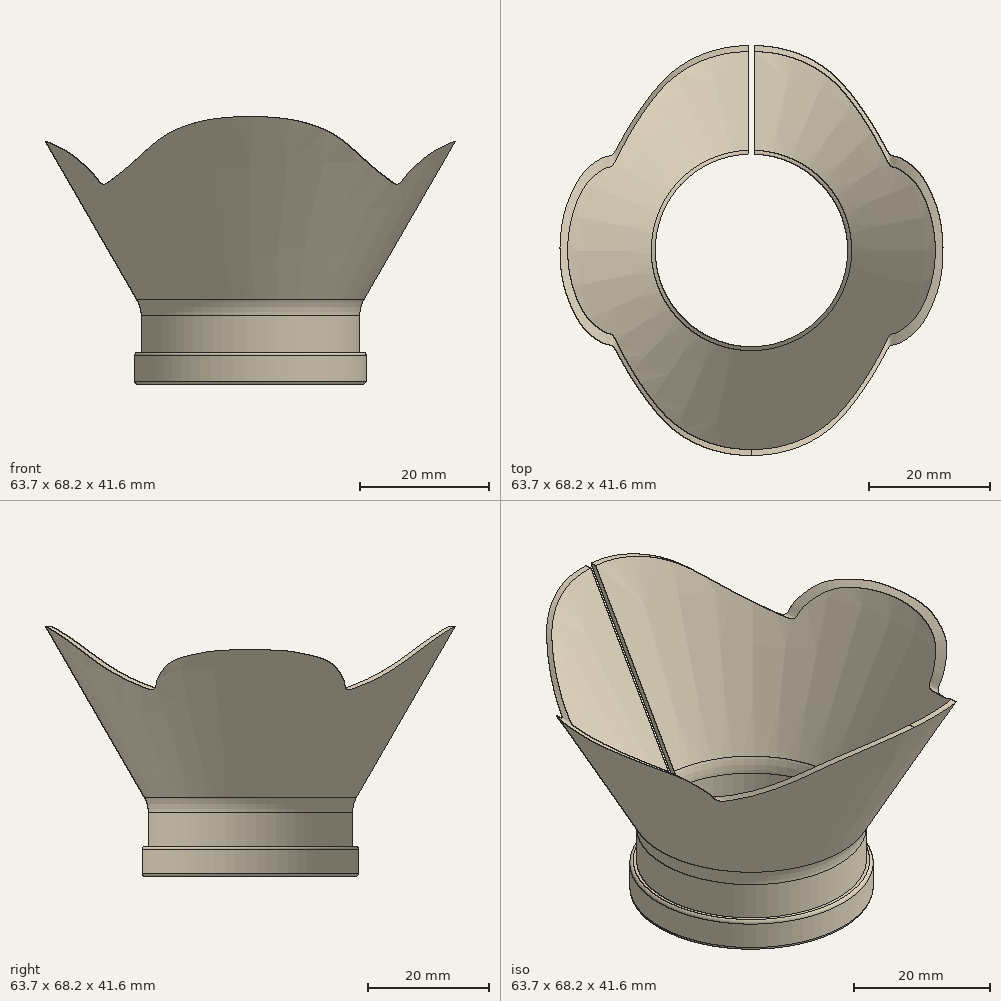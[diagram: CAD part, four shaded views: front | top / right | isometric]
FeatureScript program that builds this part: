
annotation { "Feature Type Name" : "Feature", "Feature Type Description" : "" }
export const myFeature = defineFeature(function(context is Context, id is Id, definition is map)
    precondition{}
    {
        {
            var Q0;
            Q0=qCreatedBy(makeId("Top.planeOp"),FACE);
            var sketch = newSketch(context, id + "F0", { "sketchPlane" : qUnion([Q0])});
            skCircle(sketch, "E0", {"center": v(0, 0) * mm, "radius": 16 * mm});
            skCircle(sketch, "E1.0", {"center": v(0, 0) * mm, "radius": 17 * mm});
            skSolve(sketch);
        }
        {
            var Q0;
            Q0 = qSketchRegion(id + "F0", true);
            extrude(context, id + "F1", {"entities" : qUnion([Q0]), "depth" : 12 * mm});
        }
        {
            var Q0;
            Q0=qCreatedBy(makeId("Front.planeOp"),FACE);
            var sketch = newSketch(context, id + "F2", { "sketchPlane" : qUnion([Q0])});
            skLineSegment(sketch, "E2", {"start": v(0, 0) * mm, "end": v(0, 61.93) * mm, "construction": true});
            skLineSegment(sketch, "E3.0", {"start": v(-17, 12) * mm, "end": v(17, 12) * mm, "construction": true});
            skLineSegment(sketch, "E4", {"start": v(17, 12) * mm, "end": v(34.32, 42) * mm});
            skLineSegment(sketch, "E5", {"start": v(34.32, 42) * mm, "end": v(33.57, 42.43) * mm});
            skLineSegment(sketch, "E6", {"start": v(33.57, 42.43) * mm, "end": v(16, 12) * mm});
            skLineSegment(sketch, "E7", {"start": v(16, 12) * mm, "end": v(17, 12) * mm});
            skLineSegment(sketch, "E8", {"start": v(17, 12) * mm, "end": v(17, 0) * mm, "construction": true});
            skLineSegment(sketch, "E9.bottom", {"start": v(17, 5) * mm, "end": v(18, 5) * mm});
            skLineSegment(sketch, "E9.top", {"start": v(17, 0) * mm, "end": v(18, 0) * mm});
            skLineSegment(sketch, "E9.left", {"start": v(17, 5) * mm, "end": v(17, 0) * mm});
            skLineSegment(sketch, "E9.right", {"start": v(18, 5) * mm, "end": v(18, 0) * mm});
            skSolve(sketch);
        }
        {
            var Q0;
            Q0 = qSketchRegion(id + "F2", true);
            var Q1;
            Q1=sQuery(id+"F2.wireOp",EDGE,"E2");
            revolve(context, id + "F3", {"operationType" : NewBodyOperationType.ADD, "entities" : qUnion([Q0]), "axis" : qUnion([Q1]), "revolveType" : RevolveType.FULL});
        }
        {
            var Q0;
            Q0=qCreatedBy(makeId("Front.planeOp"),FACE);
            var sketch = newSketch(context, id + "F4", { "sketchPlane" : qUnion([Q0])});
            skLineSegment(sketch, "E10.bottom", {"start": v(-60, 60.13) * mm, "end": v(60, 60.13) * mm});
            skLineSegment(sketch, "E10.top", {"start": v(-60, 27) * mm, "end": v(-45.7, 27) * mm});
            skLineSegment(sketch, "E10.left", {"start": v(-60, 60.13) * mm, "end": v(-60, 27) * mm});
            skLineSegment(sketch, "E10.right", {"start": v(60, 60.13) * mm, "end": v(60, 27) * mm});
            skPoint(sketch, "E11.0.internal.snap0", {"position": v(0, 60.13) * mm});
            skFitSpline(sketch, "E11", {"points": [v(0, 41.6) * mm, v(7.62, 40.86) * mm, v(12.88, 38.86) * mm, v(16.15, 36.34) * mm, v(19.48, 33.36) * mm, v(21.5, 31.79) * mm, v(22.87, 31.07) * mm, v(23.9, 32.05) * mm, v(25.66, 33.9) * mm, v(28.18, 35.99) * mm, v(30.49, 37.2) * mm, v(32.97, 37.6) * mm, v(45.7, 27) * mm], "startDerivative": vector(73.9, 0.28) * mm, "endDerivative": vector(56.85, -72.76) * mm});
            skFitSpline(sketch, "E12.MirrorCS", {"points": [v(0, 41.6) * mm, v(-7.62, 40.86) * mm, v(-12.88, 38.86) * mm, v(-16.15, 36.34) * mm, v(-19.48, 33.36) * mm, v(-21.5, 31.79) * mm, v(-22.87, 31.07) * mm, v(-23.9, 32.05) * mm, v(-25.66, 33.9) * mm, v(-28.18, 35.99) * mm, v(-30.49, 37.2) * mm, v(-32.97, 37.6) * mm, v(-45.7, 27) * mm], "startDerivative": vector(-73.9, 0.28) * mm, "endDerivative": vector(-56.85, -72.76) * mm});
            skLineSegment(sketch, "E13.trimOffspring", {"start": v(45.7, 27) * mm, "end": v(60, 27) * mm});
            skSolve(sketch);
        }
        {
            var Q0;
            Q0 = qSketchRegion(id + "F4", true);
            extrude(context, id + "F5", {"entities" : qUnion([Q0]), "operationType" : NewBodyOperationType.REMOVE, "endBound" : BoundingType.THROUGH_ALL, "oppositeDirection" : true, "depth" : 25 * mm, "hasSecondDirection" : true, "secondDirectionBound" : SecondDirectionBoundingType.THROUGH_ALL, "secondDirectionOppositeDirection" : false, "secondDirectionDepth" : 25 * mm});
        }
        {
            var Q0;
            Q0=qCreatedBy(makeId("Top.planeOp"),FACE);
            var sketch = newSketch(context, id + "F6", { "sketchPlane" : qUnion([Q0])});
            skLineSegment(sketch, "E14.bottom", {"start": v(0.5, 0) * mm, "end": v(-0.5, 0) * mm});
            skLineSegment(sketch, "E14.top", {"start": v(0.5, 50) * mm, "end": v(-0.5, 50) * mm});
            skLineSegment(sketch, "E14.left", {"start": v(0.5, 0) * mm, "end": v(0.5, 50) * mm});
            skLineSegment(sketch, "E14.right", {"start": v(-0.5, 0) * mm, "end": v(-0.5, 50) * mm});
            skSolve(sketch);
        }
        {
            var Q0;
            Q0 = qSketchRegion(id + "F6", true);
            extrude(context, id + "F7", {"entities" : qUnion([Q0]), "operationType" : NewBodyOperationType.REMOVE, "endBound" : BoundingType.THROUGH_ALL, "depth" : 25 * mm});
        }
        {
            var Q0;
            Q0=makeQuery(id+"F3.boolean.opBoolean","MERGE",EDGE,{"derivedFrom":[makeQuery(id+"F1.opExtrude","CAP_EDGE",EDGE,{"disambiguationData":[OSD([sQuery(id+"F0.wireOp",EDGE,"E0")])],"isStart":false}),makeQuery(id+"F3.opRevolve","SWEPT_EDGE",EDGE,{"disambiguationData":[OSD([sQuery(id+"F2.wireOp",EDGE,"E6"),sQuery(id+"F2.wireOp",EDGE,"E7")])]})]});
            fillet(context, id + "F8", {"entities" : qUnion([Q0]), "radius" : 5 * mm, "tangentPropagation" : true, "allowEdgeOverflow" : false});
        }
        {
            var Q0;
            Q0=makeQuery(id+"F3.boolean.opBoolean","MERGE",EDGE,{"derivedFrom":[makeQuery(id+"F1.opExtrude","CAP_EDGE",EDGE,{"disambiguationData":[OSD([sQuery(id+"F0.wireOp",EDGE,"E1.0")])],"isStart":false}),makeQuery(id+"F3.opRevolve","SWEPT_EDGE",EDGE,{"disambiguationData":[OSD([sQuery(id+"F2.wireOp",EDGE,"E4"),sQuery(id+"F2.wireOp",EDGE,"E7")])]})]});
            fillet(context, id + "F9", {"entities" : qUnion([Q0]), "radius" : 5 * mm, "tangentPropagation" : true, "allowEdgeOverflow" : false});
        }
        {
            var Q0;
            Q0=makeQuery(id+"F3.opRevolve","SWEPT_EDGE",EDGE,{"disambiguationData":[OSD([sQuery(id+"F2.wireOp",EDGE,"E9.bottom"),sQuery(id+"F2.wireOp",EDGE,"E9.left")])]});
            var Q1;
            Q1=makeQuery(id+"F3.opRevolve","SWEPT_EDGE",EDGE,{"disambiguationData":[OSD([sQuery(id+"F2.wireOp",EDGE,"E9.bottom"),sQuery(id+"F2.wireOp",EDGE,"E9.right")])]});
            var Q2;
            Q2=makeQuery(id+"F1.opExtrude","CAP_EDGE",EDGE,{"disambiguationData":[OSD([sQuery(id+"F0.wireOp",EDGE,"E0")])],"isStart":true});
            var Q3;
            Q3=makeQuery(id+"F3.opRevolve","SWEPT_EDGE",EDGE,{"disambiguationData":[OSD([sQuery(id+"F2.wireOp",EDGE,"E9.top"),sQuery(id+"F2.wireOp",EDGE,"E9.right")])]});
            fillet(context, id + "F10", {"entities" : qUnion([Q0, Q1, Q2, Q3]), "radius" : .5 * mm, "tangentPropagation" : true, "allowEdgeOverflow" : false});
        }
    });
